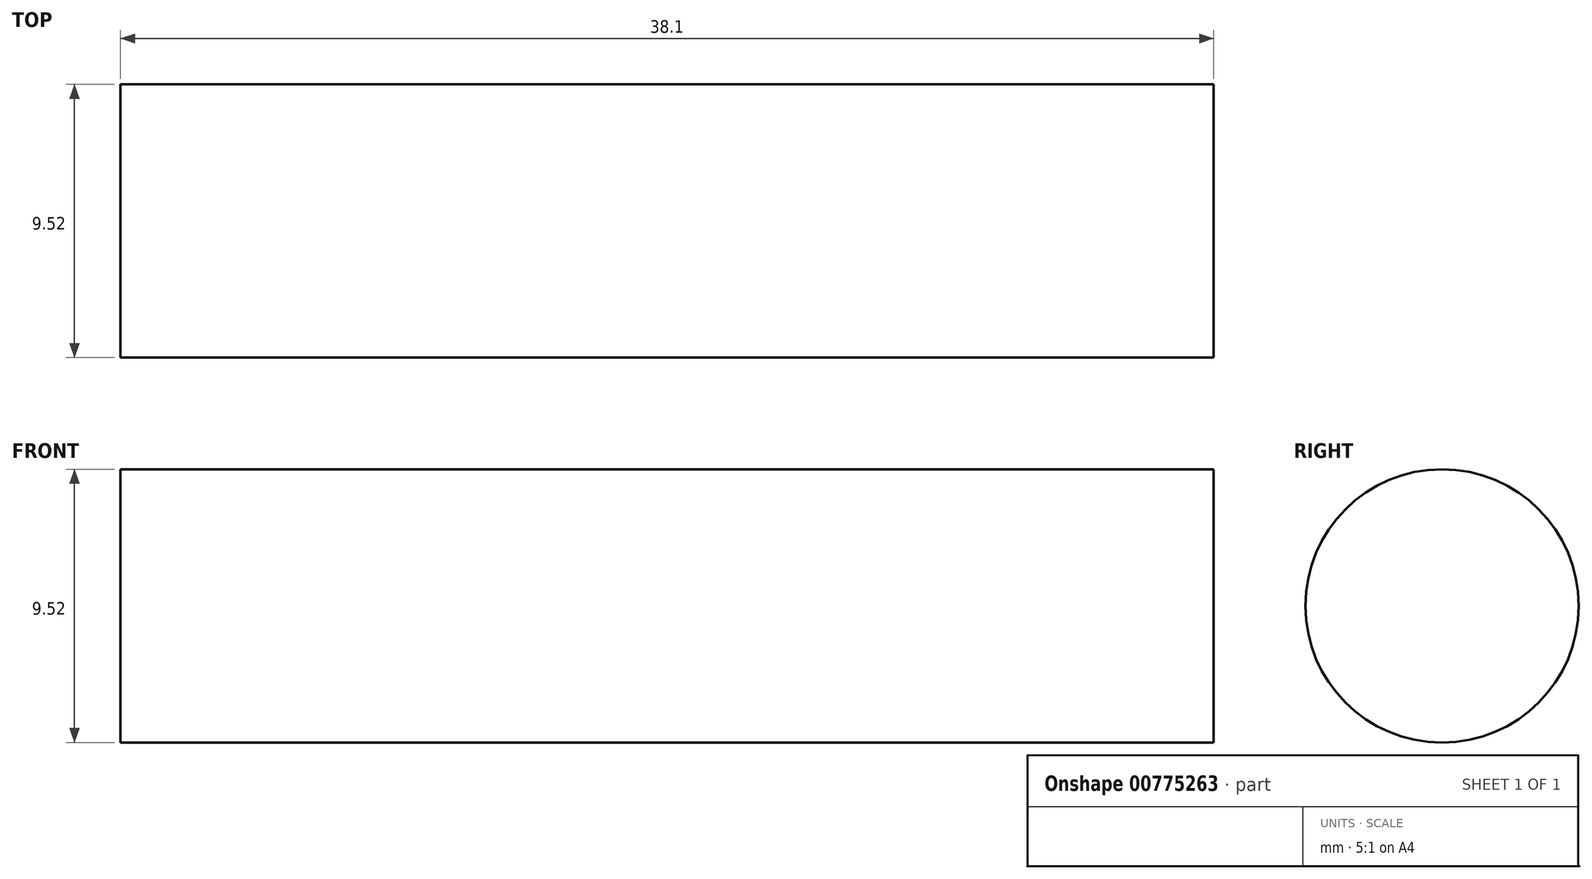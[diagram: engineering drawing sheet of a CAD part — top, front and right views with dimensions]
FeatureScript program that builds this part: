
annotation { "Feature Type Name" : "Feature", "Feature Type Description" : "" }
export const myFeature = defineFeature(function(context is Context, id is Id, definition is map)
    precondition{}
    {
        {
            var Q0;
            Q0=qCreatedBy(makeId("Right.planeOp"),FACE);
            var sketch = newSketch(context, id + "F0", { "sketchPlane" : qUnion([Q0])});
            skCircle(sketch, "E0", {"center": v(0, 0) * mm, "radius": 4.76 * mm});
            skSolve(sketch);
        }
        {
            var Q0;
            Q0 = qSketchRegion(id + "F0", true);
            extrude(context, id + "F1", {"entities" : qUnion([Q0]), "depth" : 38.1 * mm, "offsetDistance" : 25.4 * mm, "symmetric" : true});
        }
    });
